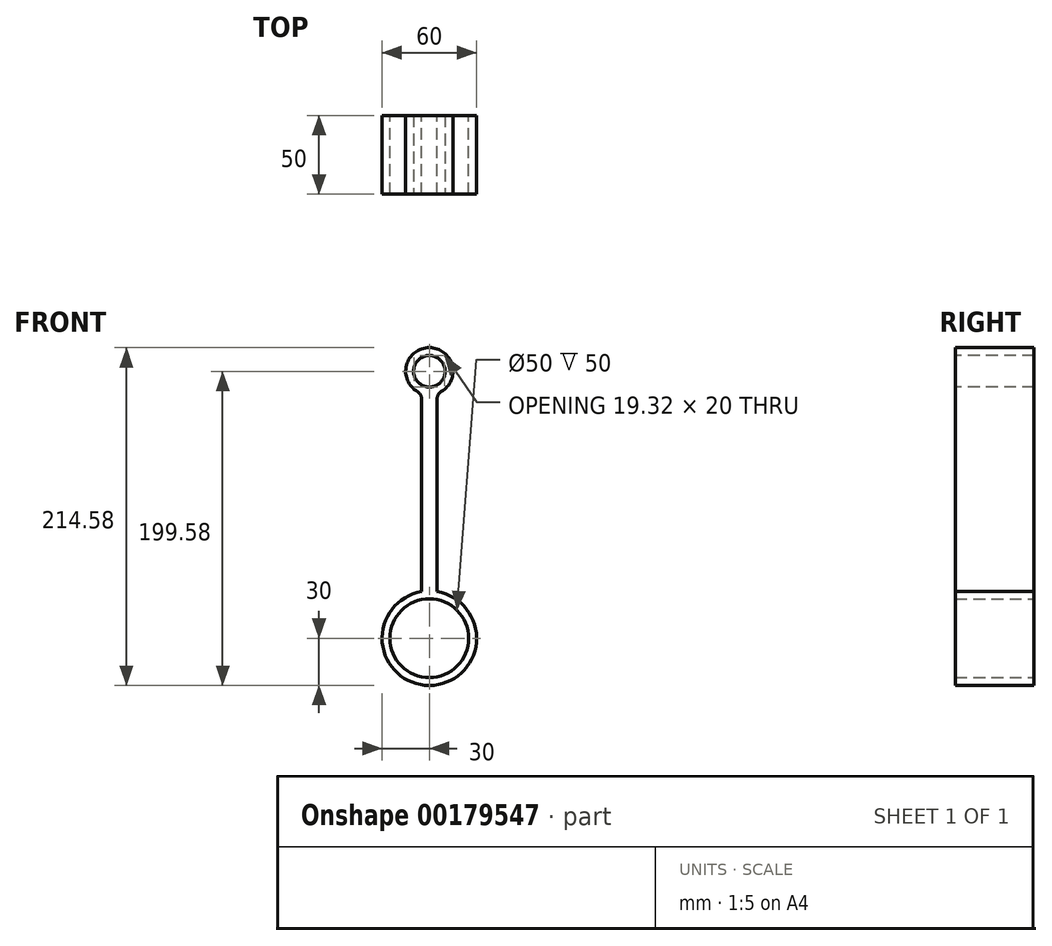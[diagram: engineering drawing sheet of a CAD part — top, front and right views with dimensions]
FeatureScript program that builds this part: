
annotation { "Feature Type Name" : "Feature", "Feature Type Description" : "" }
export const myFeature = defineFeature(function(context is Context, id is Id, definition is map)
    precondition{}
    {
        {
            var Q0;
            Q0=qCreatedBy(makeId("Front.planeOp"),FACE);
            var sketch = newSketch(context, id + "F0", { "sketchPlane" : qUnion([Q0])});
            skCircle(sketch, "E0", {"center": v(0, 0) * mm, "radius": 25 * mm});
            skCircle(sketch, "E1", {"center": v(0, 0) * mm, "radius": 30 * mm});
            skSolve(sketch);
        }
        {
            var Q0;
            Q0 = qSketchRegion(id + "F0", true);
            extrude(context, id + "F1", {"entities" : qUnion([Q0]), "depth" : 50 * mm});
        }
        {
            var Q0;
            Q0=qCreatedBy(makeId("Front.planeOp"),FACE);
            var sketch = newSketch(context, id + "F2", { "sketchPlane" : qUnion([Q0])});
            skLineSegment(sketch, "E2", {"start": v(0, -76.04) * mm, "end": v(0, 75.27) * mm, "construction": true});
            skLineSegment(sketch, "E3", {"start": v(-5, 29.58) * mm, "end": v(-5, 169.58) * mm});
            skLineSegment(sketch, "E4.MirrorCS", {"start": v(5, 29.58) * mm, "end": v(5, 169.58) * mm});
            skLineSegment(sketch, "E5", {"start": v(-5, 169.58) * mm, "end": v(5, 169.58) * mm});
            skLineSegment(sketch, "E6", {"start": v(-5, 29.58) * mm, "end": v(5, 29.58) * mm});
            skSolve(sketch);
        }
        {
            var Q0;
            Q0 = qSketchRegion(id + "F2", true);
            extrude(context, id + "F3", {"entities" : qUnion([Q0]), "operationType" : NewBodyOperationType.ADD, "flatOperationType" : FlatOperationType.REMOVE, "offsetDistance" : 25 * mm, "depth" : 50 * mm, "domain" : OperationDomain.MODEL});
        }
        {
            var Q0;
            Q0=makeQuery(id+"F3.boolean.opBoolean","MERGE",FACE,{"derivedFrom":[makeQuery(id+"F1.opExtrude","CAP_FACE",FACE,{"disambiguationData":[OSD([sQuery(id+"F0.wireOp",EDGE,"E0"),sQuery(id+"F0.wireOp",EDGE,"E1")])],"isStart":false}),makeQuery(id+"F3.opExtrude","CAP_FACE",FACE,{"disambiguationData":[OSD([sQuery(id+"F2.wireOp",EDGE,"E3"),sQuery(id+"F2.wireOp",EDGE,"E4.MirrorCS"),sQuery(id+"F2.wireOp",EDGE,"E5"),sQuery(id+"F2.wireOp",EDGE,"E6")])],"isStart":false})]});
            var sketch = newSketch(context, id + "F4", { "sketchPlane" : qUnion([Q0])});
            skCircle(sketch, "E7", {"center": v(0, 169.58) * mm, "radius": 10 * mm});
            skLineSegment(sketch, "E8", {"start": v(0, 0) * mm, "end": v(0, 169.58) * mm, "construction": true});
            skSolve(sketch);
        }
        {
            var Q0;
            Q0 = qSketchRegion(id + "F4", true);
            extrude(context, id + "F5", {"entities" : qUnion([Q0]), "operationType" : NewBodyOperationType.REMOVE, "oppositeDirection" : true, "depth" : 50 * mm});
        }
        {
            var Q0;
            Q0=makeQuery(id+"F3.boolean.opBoolean","MERGE",FACE,{"derivedFrom":[makeQuery(id+"F1.opExtrude","CAP_FACE",FACE,{"disambiguationData":[OSD([sQuery(id+"F0.wireOp",EDGE,"E0"),sQuery(id+"F0.wireOp",EDGE,"E1")])],"isStart":false}),makeQuery(id+"F3.opExtrude","CAP_FACE",FACE,{"disambiguationData":[OSD([sQuery(id+"F2.wireOp",EDGE,"E3"),sQuery(id+"F2.wireOp",EDGE,"E4.MirrorCS"),sQuery(id+"F2.wireOp",EDGE,"E5"),sQuery(id+"F2.wireOp",EDGE,"E6")])],"isStart":false})]});
            var sketch = newSketch(context, id + "F6", { "sketchPlane" : qUnion([Q0])});
            skCircle(sketch, "E9", {"center": v(0, 169.58) * mm, "radius": 15 * mm});
            skPoint(sketch, "E9.centerSnap0", {"position": v(0, 159.58) * mm});
            skCircle(sketch, "E10", {"center": v(0, 169.58) * mm, "radius": 10 * mm});
            skSolve(sketch);
        }
        {
            var Q0;
            Q0 = qSketchRegion(id + "F6", true);
            extrude(context, id + "F7", {"entities" : qUnion([Q0]), "operationType" : NewBodyOperationType.ADD, "oppositeDirection" : true, "depth" : 50 * mm});
        }
        {
            var Q0;
            Q0=makeQuery(id+"F7.boolean.opBoolean","INTERSECT",EDGE,{"derivedFrom":[makeQuery(id+"F3.opExtrude","SWEPT_FACE",FACE,{"disambiguationData":[OSD([sQuery(id+"F2.wireOp",EDGE,"E4.MirrorCS")])]}),makeQuery(id+"F7.opExtrude","SWEPT_FACE",FACE,{"disambiguationData":[OSD([sQuery(id+"F6.wireOp",EDGE,"E9")])]})]});
            var Q1;
            Q1=makeQuery(id+"F7.boolean.opBoolean","INTERSECT",EDGE,{"derivedFrom":[makeQuery(id+"F3.opExtrude","SWEPT_FACE",FACE,{"disambiguationData":[OSD([sQuery(id+"F2.wireOp",EDGE,"E3")])]}),makeQuery(id+"F7.opExtrude","SWEPT_FACE",FACE,{"disambiguationData":[OSD([sQuery(id+"F6.wireOp",EDGE,"E9")])]})]});
            var Q2;
            Q2=makeQuery(id+"F3.opExtrude","SWEPT_EDGE",EDGE,{"disambiguationData":[OSD([sQuery(id+"F2.wireOp",EDGE,"E4.MirrorCS"),sQuery(id+"F2.wireOp",EDGE,"E6")])]});
            var Q3;
            Q3=makeQuery(id+"F3.opExtrude","SWEPT_EDGE",EDGE,{"disambiguationData":[OSD([sQuery(id+"F2.wireOp",EDGE,"E3"),sQuery(id+"F2.wireOp",EDGE,"E6")])]});
            fillet(context, id + "F8", {"entities" : qUnion([Q0, Q1, Q2, Q3]), "radius" : 5 * mm, "tangentPropagation" : true, "allowEdgeOverflow" : false});
        }
    });
